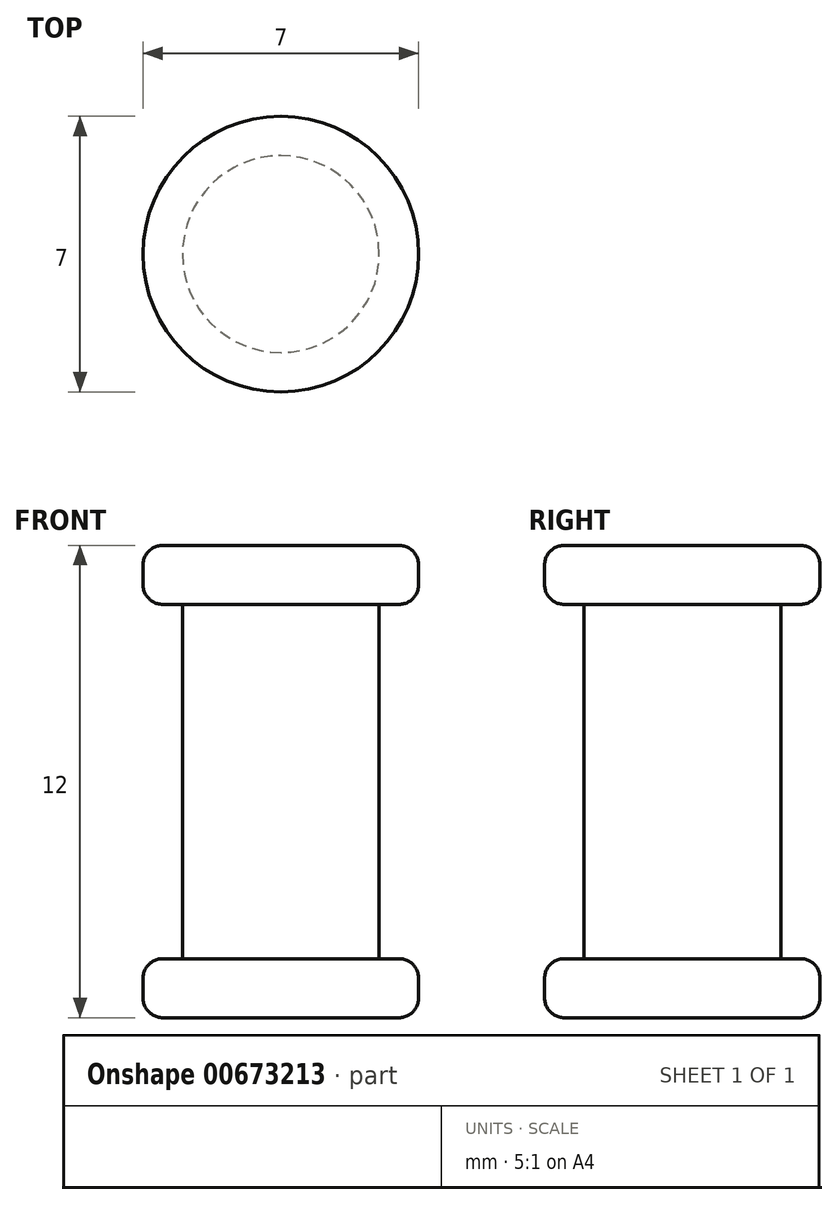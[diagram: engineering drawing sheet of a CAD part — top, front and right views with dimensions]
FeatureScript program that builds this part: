
annotation { "Feature Type Name" : "Feature", "Feature Type Description" : "" }
export const myFeature = defineFeature(function(context is Context, id is Id, definition is map)
    precondition{}
    {
        {
            var Q0;
            Q0=qCreatedBy(makeId("Right.planeOp"),FACE);
            var sketch = newSketch(context, id + "F0", { "sketchPlane" : qUnion([Q0])});
            skLineSegment(sketch, "E0", {"start": v(0, 0) * mm, "end": v(0, 16.7) * mm, "construction": true});
            skLineSegment(sketch, "E1", {"start": v(0, 0) * mm, "end": v(-3.5, 0) * mm});
            skLineSegment(sketch, "E2", {"start": v(-3.5, 0) * mm, "end": v(-3.5, 1.5) * mm});
            skLineSegment(sketch, "E3", {"start": v(-3.5, 1.5) * mm, "end": v(-2.5, 1.5) * mm});
            skLineSegment(sketch, "E4", {"start": v(-2.5, 1.5) * mm, "end": v(-2.5, 10.5) * mm});
            skLineSegment(sketch, "E5", {"start": v(-2.5, 10.5) * mm, "end": v(-3.5, 10.5) * mm});
            skLineSegment(sketch, "E6", {"start": v(-3.5, 10.5) * mm, "end": v(-3.5, 12) * mm});
            skLineSegment(sketch, "E7", {"start": v(-3.5, 12) * mm, "end": v(0, 12) * mm});
            skLineSegment(sketch, "E8", {"start": v(0, 12) * mm, "end": v(0, 0) * mm});
            skSolve(sketch);
        }
        {
            var Q0;
            Q0=qSketchRegion(id+"F0",true);
            var Q1;
            Q1=sQuery(id+"F0.wireOp",EDGE,"E8");
            revolve(context, id + "F1", {"entities" : qUnion([Q0]), "axis" : qUnion([Q1]), "revolveType" : RevolveType.FULL});
        }
        {
            var Q0;
            Q0=makeQuery(id+"F1.opRevolve","SWEPT_FACE",FACE,{"disambiguationData":[OSD([sQuery(id+"F0.wireOp",EDGE,"E6")])]});
            var Q1;
            Q1=makeQuery(id+"F1.opRevolve","SWEPT_FACE",FACE,{"disambiguationData":[OSD([sQuery(id+"F0.wireOp",EDGE,"E2")])]});
            fillet(context, id + "F2", {"entities" : qUnion([Q0, Q1]), "radius" : .5 * mm, "tangentPropagation" : true, "allowEdgeOverflow" : false});
        }
    });
